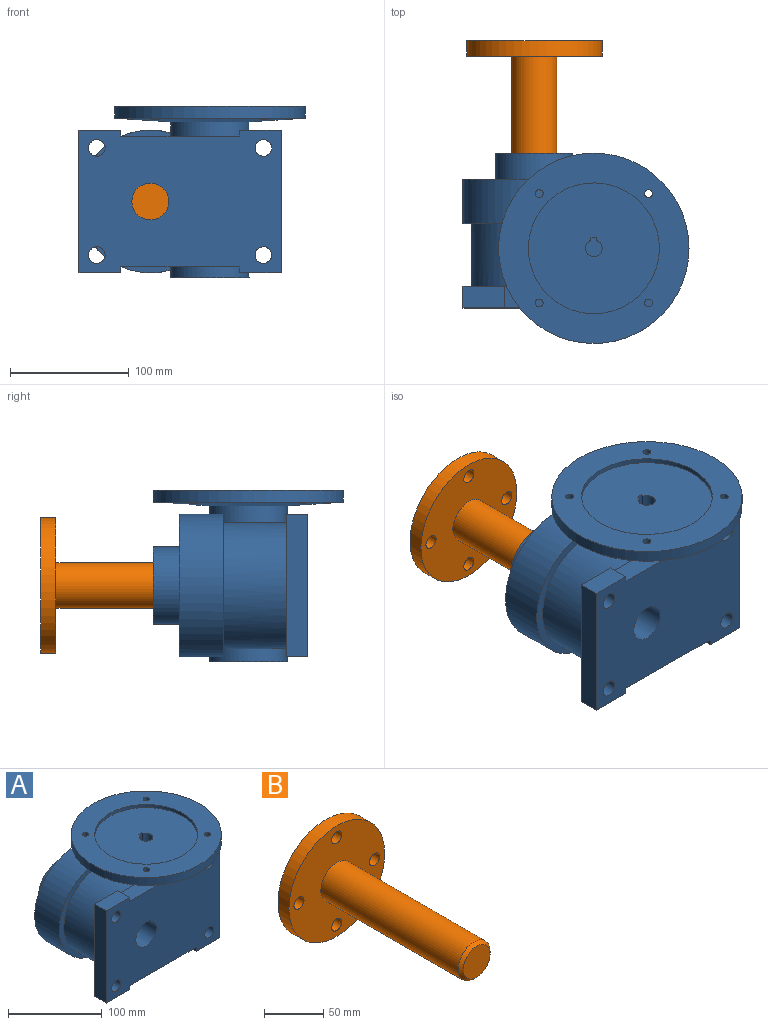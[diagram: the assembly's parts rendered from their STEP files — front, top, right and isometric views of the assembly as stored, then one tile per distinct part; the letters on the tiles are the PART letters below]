
ASSEMBLY  parts=2 mates=1
PART A: 57 faces, bbox 190x160x144 mm
  f0: cylinder r=15.5mm len=130mm, axis (0,1,0), area 12660.6mm2, adj f6,f56
  f1: plane 38.93x21.65mm, normal (0,0,-1), area 333.8mm2, adj f2,f4,f43
  f2: plane 36x21.65mm, normal (0.81,0.59,0), area 961.8mm2, adj f1,f3,f4,f43
  f3: plane 38.93x21.65mm, normal (0,0,1), area 333.8mm2, adj f2,f4,f43
  f4: cylinder r=33mm len=131mm, axis (0,0,-1), area 14825.8mm2, adj f1,f2,f3,f27,f35,f38,f39,f40
  f5: cylinder r=32.5mm len=65mm, axis (0,-1,0), area 4492.5mm2, adj f6,f45
  f6: plane 65x65mm, normal (0,1,0), area 2563.5mm2, adj f0,f5
  f7: cone r=2.09mm half-angle=59deg, axis (0,1,0), area 64.3mm2, adj f8
  f8: cylinder r=4.19mm len=12mm, axis (0,1,0), area 315.8mm2, adj f7,f45
  f9: cone r=2.09mm half-angle=59deg, axis (0,1,0), area 64.3mm2, adj f10
  f10: cylinder r=4.19mm len=12mm, axis (0,1,0), area 315.8mm2, adj f9,f45
  f11: cone r=2.09mm half-angle=59deg, axis (0,1,0), area 64.3mm2, adj f12
  f12: cylinder r=4.19mm len=12mm, axis (0,1,0), area 315.8mm2, adj f11,f45
  f13: cone r=2.09mm half-angle=59deg, axis (0,1,0), area 64.3mm2, adj f14
  f14: cylinder r=4.19mm len=12mm, axis (0,1,0), area 315.8mm2, adj f13,f45
  f15: cone r=2.09mm half-angle=59deg, axis (0,1,0), area 64.3mm2, adj f16
  f16: cylinder r=4.19mm len=12mm, axis (0,1,0), area 315.8mm2, adj f15,f45
  f17: cone r=2.09mm half-angle=59deg, axis (0,1,0), area 64.3mm2, adj f18
  f18: cylinder r=4.19mm len=12mm, axis (0,1,0), area 315.8mm2, adj f17,f45
  f19: cylinder r=7mm len=18mm, axis (0,1,0), area 791.7mm2, adj f43,f56
  f20: cylinder r=7mm len=18mm, axis (0,1,0), area 791.7mm2, adj f39,f56
  f21: cylinder r=7mm len=18mm, axis (0,1,0), area 791.7mm2, adj f39,f56
  f22: cylinder r=7mm len=18mm, axis (0,1,0), area 791.7mm2, adj f43,f56
  f23: cylinder r=3.32mm len=11.1mm, axis (0,0,1), area 230.4mm2, adj f35,f37
  f24: cylinder r=3.32mm len=11.1mm, axis (0,0,1), area 230.4mm2, adj f35,f37
  f25: cylinder r=3.32mm len=11.1mm, axis (0,0,1), area 230.4mm2, adj f35,f37
  f26: cylinder r=3.32mm len=11.1mm, axis (0,0,1), area 230.4mm2, adj f35,f37
  f27: cylinder r=60mm len=120mm, axis (0,1,0), area 13228.1mm2, adj f4,f44,f45
  f28: cylinder r=55mm len=110mm, axis (0,0,-1), area 1382.3mm2, adj f29,f37
  f29: plane 110x110mm, normal (0,0,1), area 9337.1mm2, adj f28,f30,f31,f33,f34
  f30: plane 29x5mm, normal (0,-1,0), area 145mm2, adj f29,f31,f32,f34
  f31: plane 29x2.76mm, normal (1,0,0), area 80.1mm2, adj f29,f30,f32,f33
  f32: plane 16.3x14mm, normal (0,0,1), area 166.2mm2, adj f30,f31,f33,f34
  f33: cylinder r=7mm len=29mm, axis (0,0,-1), area 1127.2mm2, adj f29,f31,f32,f34
  f34: plane 29x2.76mm, normal (-1,0,0), area 80.1mm2, adj f29,f30,f32,f33
  f35: cone r=56.5mm half-angle=86.3deg, axis (0,0,1), area 16579.4mm2, adj f4,f23,f24,f25,f26,f36
  f36: cylinder r=80mm len=160mm, axis (0,0,-1), area 5026.5mm2, adj f35,f37
  f37: plane 160x160mm, normal (0,0,1), area 10464.1mm2, adj f23,f24,f25,f26,f28,f36
  f38: plane 100x18mm, normal (0,0,1), area 1789.2mm2, adj f4,f39,f43,f47,f51,f56
  f39: plane 120x101.94mm, normal (0,1,0), area 2919.5mm2, adj f4,f20,f21,f38,f40,f42,f51,f52
  f40: cylinder r=53mm len=106mm, axis (0,1,0), area 11826.1mm2, adj f4,f39,f44
  f41: plane 66x66mm, normal (0,0,-1), area 3421.2mm2, adj f4
  f42: plane 100x18mm, normal (0,0,-1), area 1789.2mm2, adj f4,f39,f43,f46,f52,f56
  f43: plane 120x51.94mm, normal (0,1,0), area 4354mm2, adj f1,f2,f3,f4,f19,f22,f38,f42
  f44: plane 120x84.54mm, normal (0,-1,0), area 1598mm2, adj f4,f27,f40
  f45: plane 120x120mm, normal (0,1,0), area 7660.8mm2, adj f5,f8,f10,f12,f14,f16,f18,f27
  f46: plane 18x5mm, normal (-1,0,0), area 90mm2, adj f42,f43,f49,f56
  f47: plane 18x5mm, normal (-1,0,0), area 90mm2, adj f38,f43,f48,f56
  f48: plane 35x18mm, normal (0,0,1), area 630mm2, adj f43,f47,f50,f56
  f49: plane 35x18mm, normal (0,0,-1), area 630mm2, adj f43,f46,f50,f56
  f50: plane 120x18mm, normal (1,0,0), area 2160mm2, adj f43,f48,f49,f56
  f51: plane 18x5mm, normal (1,0,0), area 90mm2, adj f38,f39,f53,f56
  f52: plane 18x5mm, normal (1,0,0), area 90mm2, adj f39,f42,f55,f56
  f53: plane 35x18mm, normal (0,0,1), area 630mm2, adj f39,f51,f54,f56
  f54: plane 120x18mm, normal (-1,0,0), area 2160mm2, adj f39,f53,f55,f56
  f55: plane 35x18mm, normal (0,0,-1), area 630mm2, adj f39,f52,f54,f56
  f56: plane 170x120mm, normal (0,-1,0), area 18029.5mm2, adj f0,f19,f20,f21,f22,f38,f42,f46
PART B: 10 faces, bbox 114x179.4x114 mm
  f0: cylinder r=6mm len=13mm, axis (0,1,0), area 490.1mm2, adj f4,f9
  f1: cylinder r=6mm len=13mm, axis (0,1,0), area 490.1mm2, adj f4,f9
  f2: cylinder r=6mm len=13mm, axis (0,1,0), area 490.1mm2, adj f4,f9
  f3: cylinder r=6mm len=13mm, axis (0,1,0), area 490.1mm2, adj f4,f9
  f4: plane 114x114mm, normal (0,-1,0), area 8620.5mm2, adj f0,f1,f2,f3,f5,f7
  f5: cylinder r=57mm len=114mm, axis (0,-1,0), area 4655.8mm2, adj f4,f9
  f6: cone r=17.5mm half-angle=45deg, axis (0,1,0), area 466.5mm2, adj f7,f8
  f7: cylinder r=19mm len=163.4mm, axis (0,1,0), area 19506.8mm2, adj f4,f6
  f8: plane 32x32mm, normal (0,-1,0), area 804.2mm2, adj f6
  f9: plane 114x114mm, normal (0,1,0), area 9754.6mm2, adj f0,f1,f2,f3,f5
PLACE A at identity
PLACE B rot(axis=(0,-1,0),90deg) t=(0,45.3,0)mm
MATE slider B.f5 <-> A.f0  axis (0,1,0) through (0,130,0)mm
